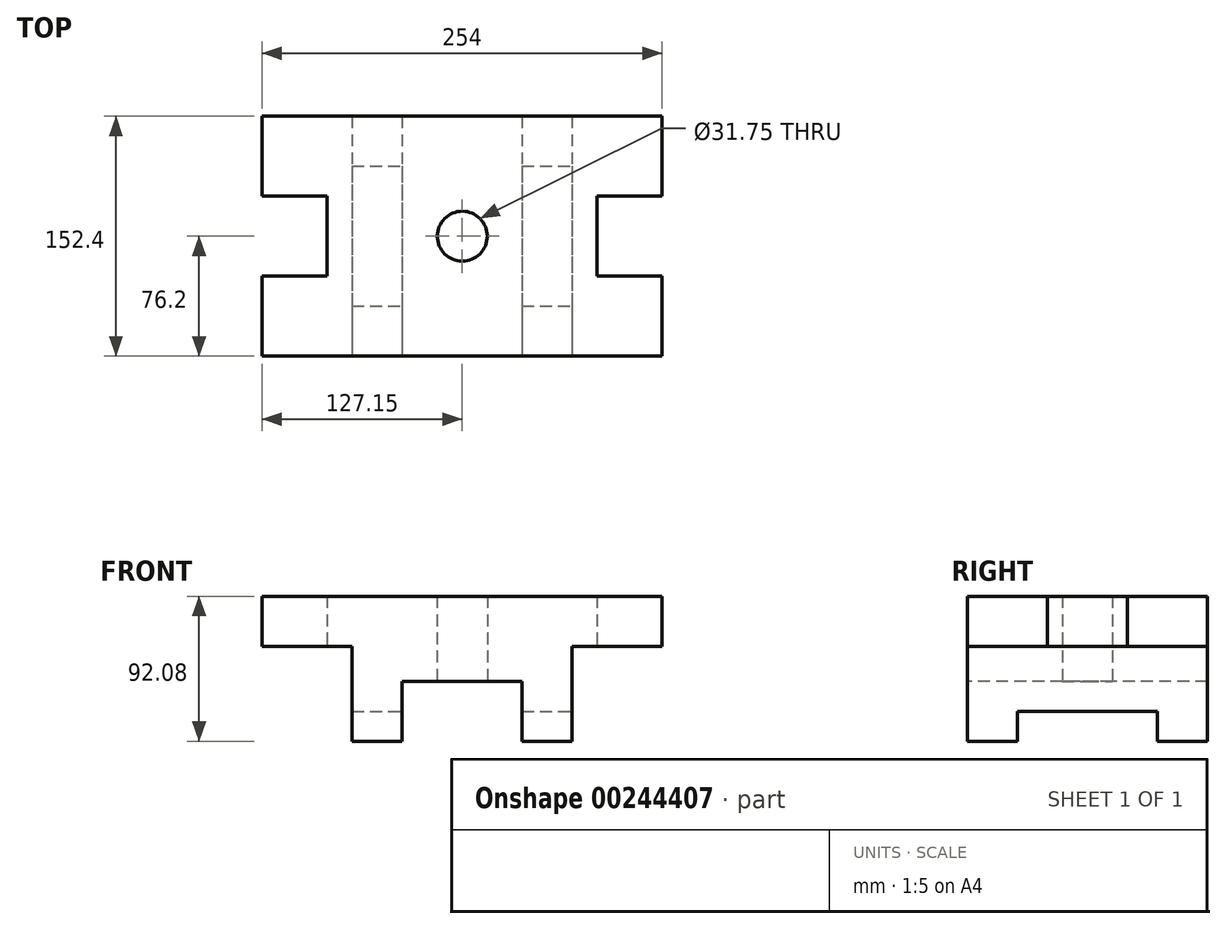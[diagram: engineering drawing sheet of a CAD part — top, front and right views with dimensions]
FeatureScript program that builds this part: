
annotation { "Feature Type Name" : "Feature", "Feature Type Description" : "" }
export const myFeature = defineFeature(function(context is Context, id is Id, definition is map)
    precondition{}
    {
        {
            var Q0;
            Q0=qCreatedBy(makeId("Top.planeOp"),FACE);
            var sketch = newSketch(context, id + "F0", { "sketchPlane" : qUnion([Q0])});
            skLineSegment(sketch, "E0.right", {"start": v(126.85, 76.2) * mm, "end": v(126.85, 25.4) * mm});
            skLineSegment(sketch, "E1.bottom", {"start": v(126.85, 25.4) * mm, "end": v(85.58, 25.4) * mm});
            skLineSegment(sketch, "E1.top", {"start": v(126.85, -25.4) * mm, "end": v(85.58, -25.4) * mm});
            skLineSegment(sketch, "E1.right", {"start": v(85.58, 25.4) * mm, "end": v(85.58, -25.4) * mm});
            skLineSegment(sketch, "E2.bottom", {"start": v(37.95, 44.45) * mm, "end": v(69.7, 44.45) * mm});
            skLineSegment(sketch, "E2.top", {"start": v(37.95, -44.45) * mm, "end": v(69.7, -44.45) * mm});
            skLineSegment(sketch, "E2.left", {"start": v(37.95, 76.2) * mm, "end": v(37.95, -76.2) * mm});
            skLineSegment(sketch, "E3.bottom", {"start": v(126.85, 76.2) * mm, "end": v(-127.15, 76.2) * mm});
            skLineSegment(sketch, "E3.right", {"start": v(-127.15, 76.2) * mm, "end": v(-127.15, 25.4) * mm});
            skLineSegment(sketch, "E4.bottom", {"start": v(-127.15, 25.4) * mm, "end": v(-85.87, 25.4) * mm});
            skLineSegment(sketch, "E4.top", {"start": v(-127.15, -25.4) * mm, "end": v(-85.87, -25.4) * mm});
            skLineSegment(sketch, "E4.right", {"start": v(-85.87, 25.4) * mm, "end": v(-85.87, -25.4) * mm});
            skLineSegment(sketch, "E5.top", {"start": v(-127.15, -76.2) * mm, "end": v(126.85, -76.2) * mm});
            skLineSegment(sketch, "E6.top", {"start": v(-70, 44.45) * mm, "end": v(-38.25, 44.45) * mm});
            skLineSegment(sketch, "E6.left", {"start": v(-70, 76.2) * mm, "end": v(-70, -76.2) * mm});
            skLineSegment(sketch, "E7.bottom", {"start": v(-70, -44.45) * mm, "end": v(-38.25, -44.45) * mm});
            skLineSegment(sketch, "E7.right", {"start": v(-38.25, 76.2) * mm, "end": v(-38.25, -76.2) * mm});
            skCircle(sketch, "E8", {"center": v(0, 0) * mm, "radius": 15.88 * mm});
            skLineSegment(sketch, "E9.trimOffspring", {"start": v(126.85, -25.4) * mm, "end": v(126.85, -76.2) * mm});
            skLineSegment(sketch, "E10.trimOffspring", {"start": v(-127.15, -25.4) * mm, "end": v(-127.15, -76.2) * mm});
            skLineSegment(sketch, "E11", {"start": v(69.7, 76.2) * mm, "end": v(69.7, -76.2) * mm});
            skSolve(sketch);
        }
        {
            var Q0;
            Q0 = qSketchRegion(id + "F0", true);
            var Q1;
            {var subQ0=sQuery(id+"F0.wireOp",EDGE,"E6.top");Q1=makeQuery(id+"F0.imprint","IMPRINT",FACE,{"disambiguationData":[TD([[makeQuery(id+"F0.imprint","IMPRINT",EDGE,{"derivedFrom":subQ0}),-1.0]])]});}
            var Q2;
            {var subQ0=sQuery(id+"F0.wireOp",EDGE,"E2.bottom");Q2=makeQuery(id+"F0.imprint","IMPRINT",FACE,{"disambiguationData":[TD([[makeQuery(id+"F0.imprint","IMPRINT",EDGE,{"derivedFrom":subQ0}),-1.0]])]});}
            extrude(context, id + "F1", {"entities" : qUnion([Q0, Q1, Q2]), "depth" : 92.07 * mm});
        }
        {
            var Q0;
            {var subQ0=sQuery(id+"F0.wireOp",EDGE,"E6.top");Q0=makeQuery(id+"F0.imprint","IMPRINT",FACE,{"disambiguationData":[TD([[makeQuery(id+"F0.imprint","IMPRINT",EDGE,{"derivedFrom":subQ0}),-1.0]])]});}
            var Q1;
            {var subQ0=sQuery(id+"F0.wireOp",EDGE,"E2.bottom");Q1=makeQuery(id+"F0.imprint","IMPRINT",FACE,{"disambiguationData":[TD([[makeQuery(id+"F0.imprint","IMPRINT",EDGE,{"derivedFrom":subQ0}),-1.0]])]});}
            extrude(context, id + "F2", {"entities" : qUnion([Q0, Q1]), "operationType" : NewBodyOperationType.REMOVE, "depth" : 19.05 * mm});
        }
        {
            var Q0;
            Q0=makeQuery(id+"F0.imprint","IMPRINT",FACE,{"disambiguationData":[TD([[makeQuery(id+"F0.imprint","IMPRINT",EDGE,{"derivedFrom":sQuery(id+"F0.wireOp",EDGE,"E8")}),-1.0]])]});
            extrude(context, id + "F3", {"entities" : qUnion([Q0]), "operationType" : NewBodyOperationType.REMOVE, "depth" : 38.1 * mm});
        }
        {
            var Q0;
            {var subQ4=sQuery(id+"F0.wireOp",EDGE,"E3.right");Q0=makeQuery(id+"F0.imprint","IMPRINT",FACE,{"disambiguationData":[TD([[makeQuery(id+"F0.imprint","IMPRINT",EDGE,{"derivedFrom":subQ4}),1.0]])]});}
            var Q1;
            {var subQ1=sQuery(id+"F0.wireOp",EDGE,"E0.right");Q1=makeQuery(id+"F0.imprint","IMPRINT",FACE,{"disambiguationData":[TD([[makeQuery(id+"F0.imprint","IMPRINT",EDGE,{"derivedFrom":subQ1}),-1.0]])]});}
            extrude(context, id + "F4", {"entities" : qUnion([Q0, Q1]), "operationType" : NewBodyOperationType.REMOVE, "depth" : 60.32 * mm});
        }
    });
